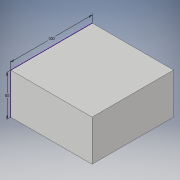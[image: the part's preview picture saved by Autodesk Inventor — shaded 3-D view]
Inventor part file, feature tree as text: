
AUTODESK INVENTOR PART (.ipt)
format: ipt  version: 2019.3 (Build 233278000, 278)  size: 87,552 bytes
history: native  units: mm
features: other x1, extrude x1, sketch x1
ambient origin geometry x8: Origin, YZ Plane, XZ Plane, XY Plane, X Axis, Y Axis, Z Axis, Center Point
bodies: Body1 (feature_tree)
feature tree (3):
  other  "ソリッド1"
  extrude  "押し出し1"  Depth=50.0mm
  sketch  "スケッチ1"
